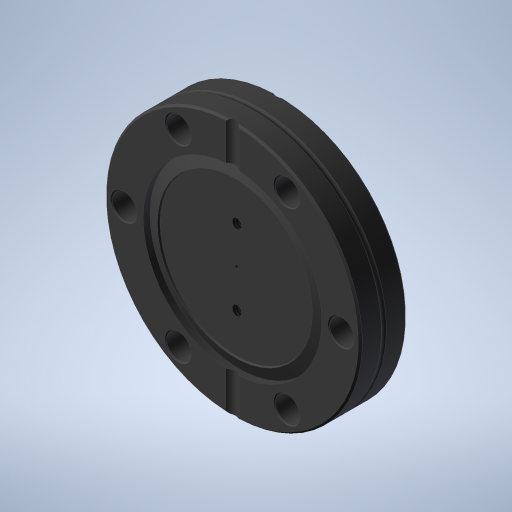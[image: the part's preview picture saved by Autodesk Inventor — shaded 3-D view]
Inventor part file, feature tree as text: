
AUTODESK INVENTOR PART (.ipt)
format: ipt  version: 2024 (Build 280153000, 153)  size: 352,768 bytes
history: native  units: in
note: dims shown in document units (in); Inventor stores cm internally (conversion verified against a paired STEP export)
features: hole x2, sketch x1
ambient origin geometry x8: Origin, YZ Plane, XZ Plane, XY Plane, X Axis, Y Axis, Z Axis, Center Point
bodies: Solid1 (feature_tree)
feature tree (3):
  sketch  "Sketch1"  dims[d2=0.4in d4=0.104in d5=0.25in d6=0.279in d7=0.25in d8=0.5635in d9=0.25in d10=0.0in d11=0.04in d12=0.25in d13=0.375in d14=0.25in d15=0.5635in d16=0.25in d17=0.0in]
  hole  "Hole1"  [1 undecoded]
  hole  "Hole2"  [1 undecoded]
note: 2 required parameter values undecoded (feature->parameter linkage not recoverable at this tier; creation-order binding heuristic only, values carry confidence <= 0.55)
